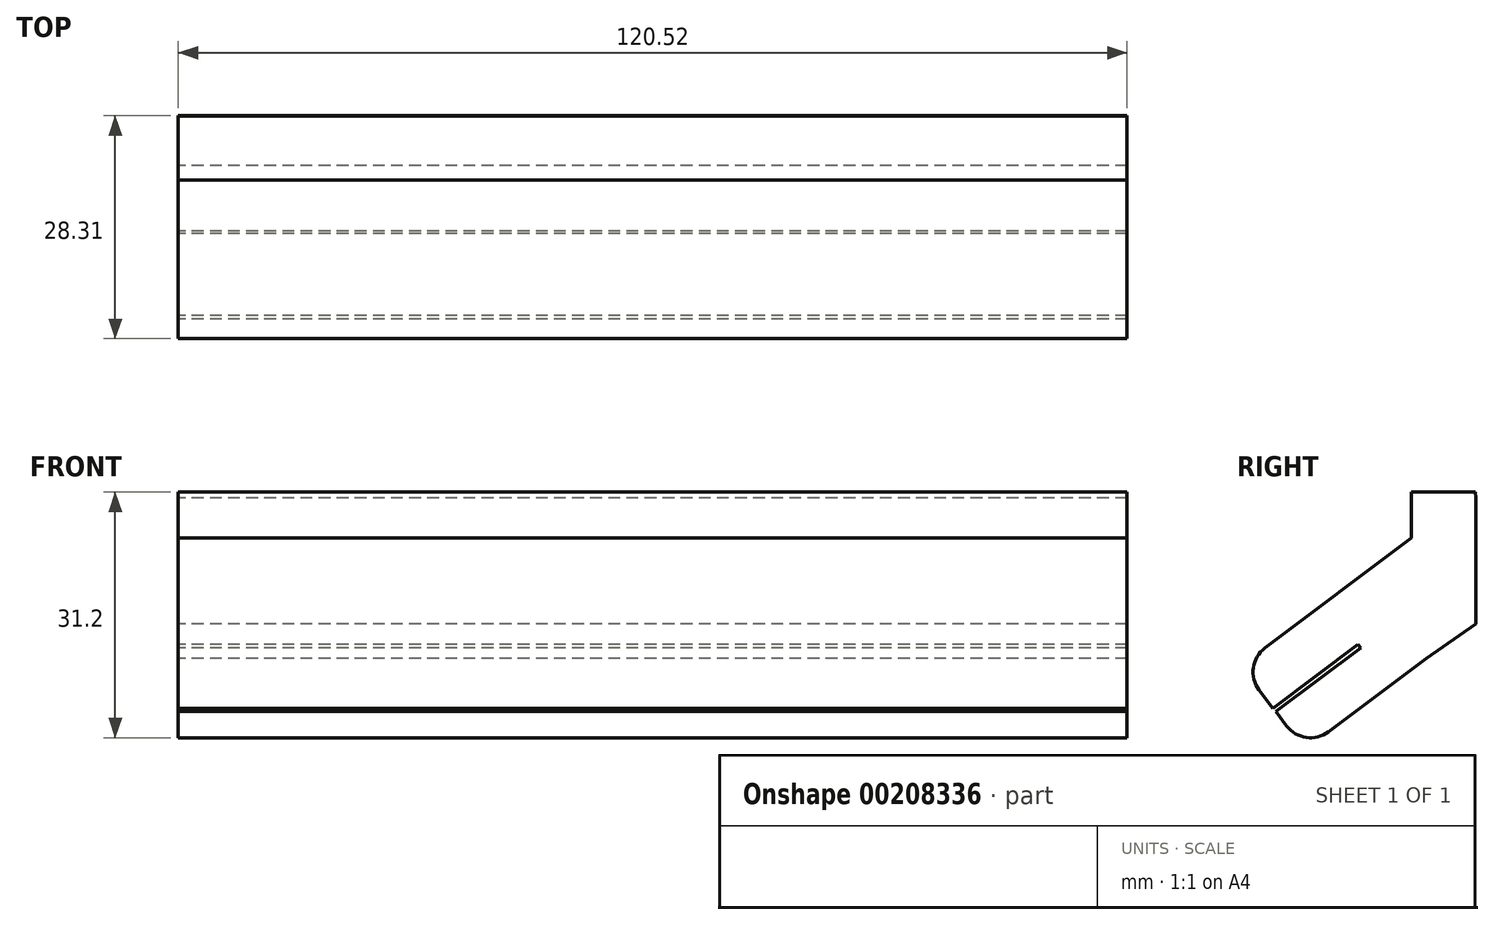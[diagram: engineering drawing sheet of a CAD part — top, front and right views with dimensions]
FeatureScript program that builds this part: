
annotation { "Feature Type Name" : "Feature", "Feature Type Description" : "" }
export const myFeature = defineFeature(function(context is Context, id is Id, definition is map)
    precondition{}
    {
        {
            var Q0;
            Q0=qCreatedBy(makeId("Right.planeOp"),FACE);
            var sketch = newSketch(context, id + "F0", { "sketchPlane" : qUnion([Q0])});
            skLineSegment(sketch, "E0", {"start": v(0, 16.25) * mm, "end": v(-21.67, 0) * mm});
            skLineSegment(sketch, "E1", {"start": v(-21.67, 0) * mm, "end": v(-17.62, -5.4) * mm});
            skLineSegment(sketch, "E2", {"start": v(-17.62, -5.4) * mm, "end": v(-6.8, 2.72) * mm});
            skLineSegment(sketch, "E3", {"start": v(-6.8, 2.72) * mm, "end": v(-6.47, 2.28) * mm});
            skLineSegment(sketch, "E4", {"start": v(-6.47, 2.28) * mm, "end": v(-17.23, -5.79) * mm});
            skLineSegment(sketch, "E5", {"start": v(-17.23, -5.79) * mm, "end": v(-13.6, -10.64) * mm});
            skLineSegment(sketch, "E6", {"start": v(-13.6, -10.64) * mm, "end": v(1.86, 0.96) * mm});
            skLineSegment(sketch, "E7", {"start": v(0, 16.25) * mm, "end": v(8.17, 5.35) * mm});
            skLineSegment(sketch, "E8", {"start": v(8.17, 5.35) * mm, "end": v(1.86, 0.96) * mm});
            skLineSegment(sketch, "E9", {"start": v(0, 16.25) * mm, "end": v(0, 22.09) * mm});
            skLineSegment(sketch, "E10", {"start": v(8.17, 5.35) * mm, "end": v(8.17, 21.35) * mm});
            skLineSegment(sketch, "E11", {"start": v(0, 22.09) * mm, "end": v(8.13, 22.09) * mm});
            skLineSegment(sketch, "E12", {"start": v(8.13, 22.09) * mm, "end": v(8.17, 21.35) * mm});
            skSolve(sketch);
        }
        {
            var Q0;
            Q0=makeQuery(id+"F0.imprint","IMPRINT",FACE,{"disambiguationData":[TD([[makeQuery(id+"F0.imprint","IMPRINT",EDGE,{"derivedFrom":sQuery(id+"F0.wireOp",EDGE,"E0")}),1.0]])]});
            var Q1;
            Q1=makeQuery(id+"F0.imprint","IMPRINT",FACE,{"disambiguationData":[TD([[makeQuery(id+"F0.imprint","IMPRINT",EDGE,{"derivedFrom":sQuery(id+"F0.wireOp",EDGE,"E7")}),1.0]])]});
            extrude(context, id + "F1", {"entities" : qUnion([Q0, Q1]), "depth" : 120.52 * mm});
        }
        {
            var Q0;
            Q0=makeQuery(id+"F1.opExtrude","SWEPT_EDGE",EDGE,{"disambiguationData":[OSD([sQuery(id+"F0.wireOp",EDGE,"E0"),sQuery(id+"F0.wireOp",EDGE,"E1")])]});
            var Q1;
            Q1=makeQuery(id+"F1.opExtrude","SWEPT_EDGE",EDGE,{"disambiguationData":[OSD([sQuery(id+"F0.wireOp",EDGE,"E5"),sQuery(id+"F0.wireOp",EDGE,"E6")])]});
            fillet(context, id + "F2", {"entities" : qUnion([Q0, Q1]), "radius" : 3.8 * mm, "tangentPropagation" : true, "allowEdgeOverflow" : false});
        }
    });
